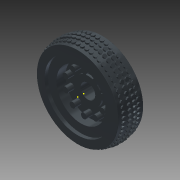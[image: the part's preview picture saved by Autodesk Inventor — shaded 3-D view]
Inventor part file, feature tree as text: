
AUTODESK INVENTOR PART (.ipt)
format: ipt  version: 2015 (Build 190159000, 159)  size: 3,270,656 bytes
history: native  units: in
note: dims shown in document units (in); Inventor stores cm internally (conversion verified against a paired STEP export)
features: other x3, sketch x3, extrude x1
ambient origin geometry x8: Origin, YZ Plane, XZ Plane, XY Plane, X Axis, Y Axis, Z Axis, Center Point
bodies: Solid1 (feature_tree)
feature tree (7):
  other  "Part3 (1).ipt"
  extrude  "Extrusion1"  Depth=0.3543in
  other  "Solid1::Part3 (1).ipt"
  other  "TaggingFeature1"
  sketch  "Sketch14"
  sketch  "Sketch3"  dims[d0=0.3543in d1=0.35in]
  sketch  "Sketch4"  dims[d2=1.0in d3=0.0in]
